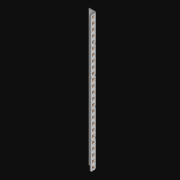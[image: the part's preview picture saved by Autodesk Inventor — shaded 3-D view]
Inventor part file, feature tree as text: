
AUTODESK INVENTOR PART (.ipt)
format: ipt  version: 2021 (Build 250183000, 183)  size: 1,260,032 bytes
history: native  units: in
note: dims shown in document units (in); Inventor stores cm internally (conversion verified against a paired STEP export)
features: extrude x52, other x50, sketch x4, pattern_linear x2, sheet_metal_op x1
ambient origin geometry x8: Origin, YZ Plane, XZ Plane, XY Plane, X Axis, Y Axis, Z Axis, Center Point
bodies: Solid1 (feature_tree)
feature tree (109):
  pattern_linear  "Rectangular Pattern1"  Spacing1=0.5in  [1 undecoded]
  pattern_linear  "Rectangular Pattern3"  Count1=25  [1 undecoded]
  extrude  "Extrusion1"  Depth=0.5in
  extrude  "Extrusion2"  Depth=0.5in
  sketch  "Sketch1"  dims[d0=0.182in]
  other  "Srf1"
  sketch  "Sketch3"  dims[d1=0.063in d2=0.0in]
  other  "Srf3"
  other  "Srf4"
  other  "Srf5"
  other  "Srf6"
  other  "Srf7"
  other  "Srf8"
  other  "Srf9"
  other  "Srf10"
  other  "Srf11"
  other  "Srf12"
  other  "Srf13"
  other  "Srf14"
  other  "Srf15"
  other  "Srf16"
  other  "Srf17"
  other  "Srf18"
  other  "Srf19"
  other  "Srf20"
  other  "Srf21"
  other  "Srf22"
  other  "Srf23"
  other  "Srf24"
  other  "Srf25"
  other  "Srf26"
  other  "Srf27"
  other  "Srf142"
  other  "Srf143"
  other  "Srf144"
  other  "Srf145"
  other  "Srf146"
  other  "Srf147"
  other  "Srf148"
  other  "Srf149"
  other  "Srf150"
  other  "Srf151"
  other  "Srf152"
  other  "Srf153"
  other  "Srf154"
  other  "Srf155"
  other  "Srf156"
  other  "Srf157"
  other  "Srf158"
  other  "Srf159"
  other  "Srf160"
  other  "Srf161"
  other  "Srf162"
  other  "Srf163"
  other  "Srf164"
  other  "Srf165"
  sketch  "Sketch4"  dims[d6=0.182in]
  sketch  "Sketch5"  dims[d7=0.063in d8=0.0in d11=0.5in d12=0.3937in d14=0.5in d18=9.8425in d20=0.5in d21=5.0in d22=0.0in d23=0.841in d24=0.0in]
  sheet_metal_op  "Fold1"
  extrude  "ExtrusionSrf1"  TaperAngle=0.0deg  [1 undecoded]
  extrude  "ExtrusionSrf3"  Depth=0.5in TaperAngle=0.0deg
  extrude  "ExtrusionSrf4"  [1 undecoded]
  extrude  "ExtrusionSrf5"  [1 undecoded]
  extrude  "ExtrusionSrf6"  [1 undecoded]
  extrude  "ExtrusionSrf7"  [1 undecoded]
  extrude  "ExtrusionSrf8"  [1 undecoded]
  extrude  "ExtrusionSrf9"  [1 undecoded]
  extrude  "ExtrusionSrf10"  [1 undecoded]
  extrude  "ExtrusionSrf11"  [1 undecoded]
  extrude  "ExtrusionSrf12"  [1 undecoded]
  extrude  "ExtrusionSrf13"  [1 undecoded]
  extrude  "ExtrusionSrf14"  [1 undecoded]
  extrude  "ExtrusionSrf15"  [1 undecoded]
  extrude  "ExtrusionSrf16"  [1 undecoded]
  extrude  "ExtrusionSrf17"  [1 undecoded]
  extrude  "ExtrusionSrf18"  [1 undecoded]
  extrude  "ExtrusionSrf19"  [1 undecoded]
  extrude  "ExtrusionSrf20"  [1 undecoded]
  extrude  "ExtrusionSrf21"  [1 undecoded]
  extrude  "ExtrusionSrf22"  [1 undecoded]
  extrude  "ExtrusionSrf23"  [1 undecoded]
  extrude  "ExtrusionSrf24"  [1 undecoded]
  extrude  "ExtrusionSrf25"  [1 undecoded]
  extrude  "ExtrusionSrf26"  [1 undecoded]
  extrude  "ExtrusionSrf27"  [1 undecoded]
  extrude  "ExtrusionSrf142"  [1 undecoded]
  extrude  "ExtrusionSrf143"  [1 undecoded]
  extrude  "ExtrusionSrf144"  [1 undecoded]
  extrude  "ExtrusionSrf145"  [1 undecoded]
  extrude  "ExtrusionSrf146"  [1 undecoded]
  extrude  "ExtrusionSrf147"  [1 undecoded]
  extrude  "ExtrusionSrf148"  [1 undecoded]
  extrude  "ExtrusionSrf149"  [1 undecoded]
  extrude  "ExtrusionSrf150"  [1 undecoded]
  extrude  "ExtrusionSrf151"  [1 undecoded]
  extrude  "ExtrusionSrf152"  [1 undecoded]
  extrude  "ExtrusionSrf153"  [1 undecoded]
  extrude  "ExtrusionSrf154"  [1 undecoded]
  extrude  "ExtrusionSrf155"  [1 undecoded]
  extrude  "ExtrusionSrf156"  [1 undecoded]
  extrude  "ExtrusionSrf157"  [1 undecoded]
  extrude  "ExtrusionSrf158"  [1 undecoded]
  extrude  "ExtrusionSrf159"  [1 undecoded]
  extrude  "ExtrusionSrf160"  [1 undecoded]
  extrude  "ExtrusionSrf161"  [1 undecoded]
  extrude  "ExtrusionSrf162"  [1 undecoded]
  extrude  "ExtrusionSrf163"  [1 undecoded]
  extrude  "ExtrusionSrf164"  [1 undecoded]
  extrude  "ExtrusionSrf165"  [1 undecoded]
note: 51 required parameter values undecoded (feature->parameter linkage not recoverable at this tier; creation-order binding heuristic only, values carry confidence <= 0.55)
